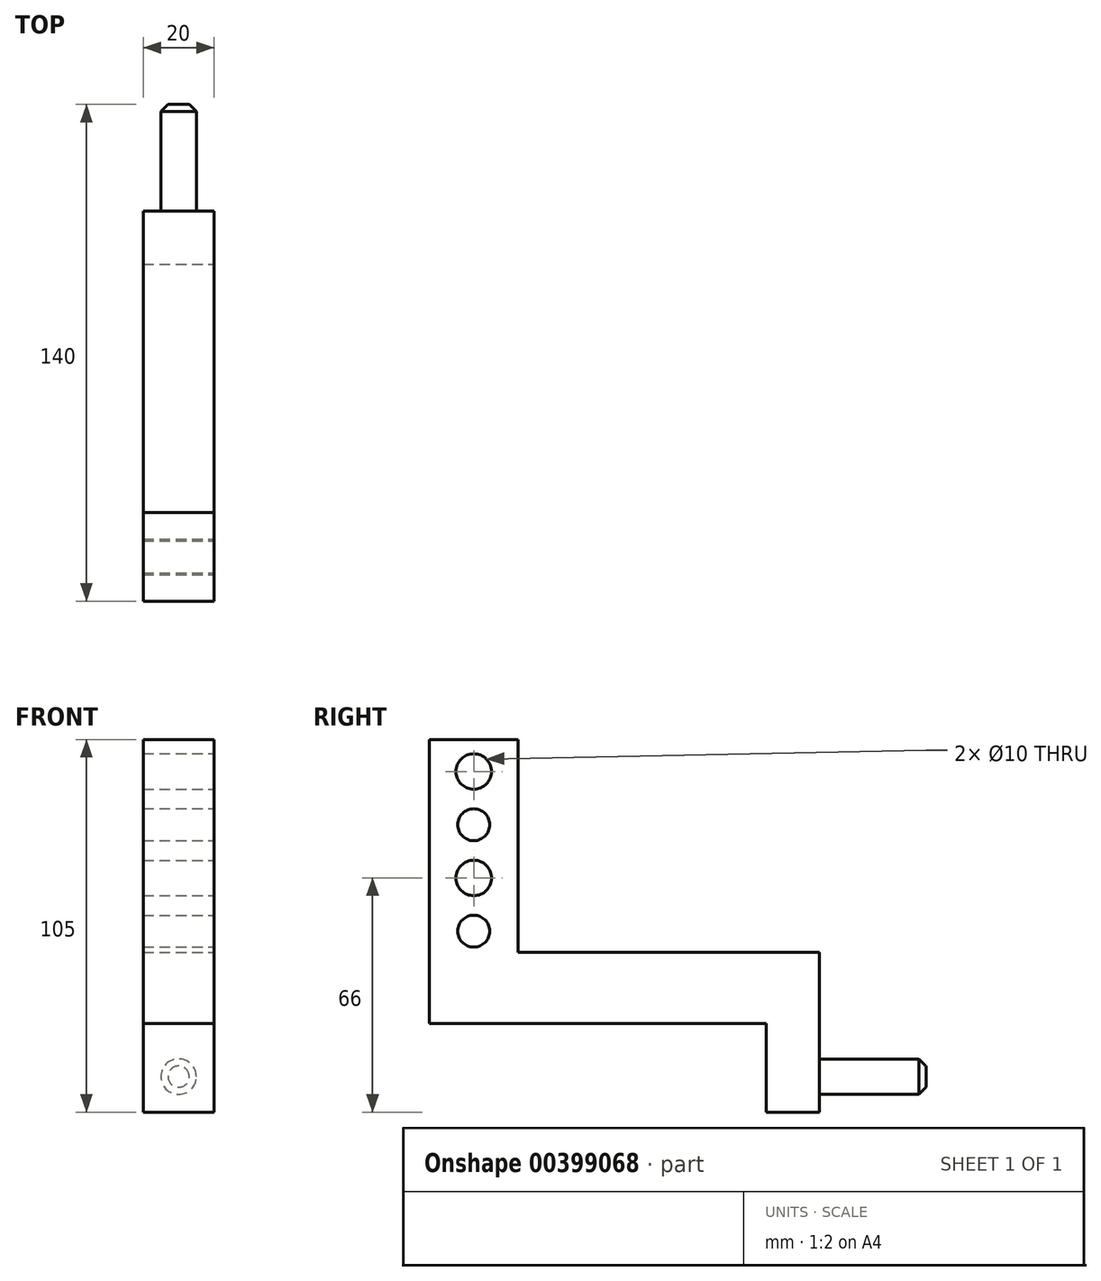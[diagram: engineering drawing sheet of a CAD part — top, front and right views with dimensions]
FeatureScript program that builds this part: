
annotation { "Feature Type Name" : "Feature", "Feature Type Description" : "" }
export const myFeature = defineFeature(function(context is Context, id is Id, definition is map)
    precondition{}
    {
        {
            var Q0;
            Q0=qCreatedBy(makeId("Top.planeOp"),FACE);
            var sketch = newSketch(context, id + "F0", { "sketchPlane" : qUnion([Q0])});
            skLineSegment(sketch, "E0.bottom", {"start": v(0, 0) * mm, "end": v(20, 0) * mm});
            skLineSegment(sketch, "E0.top", {"start": v(0, -25) * mm, "end": v(20, -25) * mm});
            skLineSegment(sketch, "E0.left", {"start": v(0, 0) * mm, "end": v(0, -25) * mm});
            skLineSegment(sketch, "E0.right", {"start": v(20, 0) * mm, "end": v(20, -25) * mm});
            skSolve(sketch);
        }
        {
            var Q0;
            Q0 = qSketchRegion(id + "F0", true);
            extrude(context, id + "F1", {"entities" : qUnion([Q0]), "depth" : 80 * mm});
        }
        {
            var Q0;
            Q0=makeQuery(id+"F1.opExtrude","SWEPT_FACE",FACE,{"disambiguationData":[OSD([sQuery(id+"F0.wireOp",EDGE,"E0.right")])]});
            var sketch = newSketch(context, id + "F2", { "sketchPlane" : qUnion([Q0])});
            skLineSegment(sketch, "E1", {"start": v(-12.5, 80) * mm, "end": v(-12.5, 71) * mm, "construction": true});
            skPoint(sketch, "E1.endSnap0", {"position": v(-12.5, 80) * mm});
            skLineSegment(sketch, "E2", {"start": v(-12.5, 71) * mm, "end": v(-12.5, 56) * mm, "construction": true});
            skLineSegment(sketch, "E3", {"start": v(-12.5, 56) * mm, "end": v(-12.5, 41) * mm, "construction": true});
            skLineSegment(sketch, "E4", {"start": v(-12.5, 41) * mm, "end": v(-12.5, 26) * mm, "construction": true});
            skLineSegment(sketch, "E5", {"start": v(-12.5, 26) * mm, "end": v(-12.5, 0) * mm, "construction": true});
            skCircle(sketch, "E6", {"center": v(-12.5, 71) * mm, "radius": 5 * mm});
            skCircle(sketch, "E7", {"center": v(-12.5, 56) * mm, "radius": 4.5 * mm});
            skCircle(sketch, "E8", {"center": v(-12.5, 41) * mm, "radius": 5 * mm});
            skCircle(sketch, "E9", {"center": v(-12.5, 26) * mm, "radius": 4.5 * mm});
            skSolve(sketch);
        }
        {
            var Q0;
            Q0 = qSketchRegion(id + "F2", true);
            extrude(context, id + "F3", {"entities" : qUnion([Q0]), "operationType" : NewBodyOperationType.REMOVE, "oppositeDirection" : true, "depth" : 25 * mm});
        }
        {
            var Q0;
            Q0=makeQuery(id+"F1.opExtrude","SWEPT_FACE",FACE,{"disambiguationData":[OSD([sQuery(id+"F0.wireOp",EDGE,"E0.bottom")])]});
            var sketch = newSketch(context, id + "F4", { "sketchPlane" : qUnion([Q0])});
            skLineSegment(sketch, "E10.bottom", {"start": v(0, 0) * mm, "end": v(-20, 0) * mm});
            skLineSegment(sketch, "E10.top", {"start": v(0, 20) * mm, "end": v(-20, 20) * mm});
            skLineSegment(sketch, "E10.left", {"start": v(0, 0) * mm, "end": v(0, 20) * mm});
            skLineSegment(sketch, "E10.right", {"start": v(-20, 0) * mm, "end": v(-20, 20) * mm});
            skSolve(sketch);
        }
        {
            var Q0;
            Q0=makeQuery(id+"F4.imprint","IMPRINT",FACE,{"disambiguationData":[TD([[makeQuery(id+"F4.imprint","IMPRINT",EDGE,{"derivedFrom":sQuery(id+"F4.wireOp",EDGE,"E10.bottom")}),-1.0]])]});
            extrude(context, id + "F5", {"entities" : qUnion([Q0]), "operationType" : NewBodyOperationType.ADD, "depth" : 70 * mm});
        }
        {
            var Q0;
            Q0=makeQuery(id+"F5.opExtrude","CAP_FACE",FACE,{"disambiguationData":[OSD([sQuery(id+"F4.wireOp",EDGE,"E10.bottom"),sQuery(id+"F4.wireOp",EDGE,"E10.top"),sQuery(id+"F4.wireOp",EDGE,"E10.left"),sQuery(id+"F4.wireOp",EDGE,"E10.right")])],"isStart":false});
            var sketch = newSketch(context, id + "F6", { "sketchPlane" : qUnion([Q0])});
            skLineSegment(sketch, "E11.bottom", {"start": v(-20, 20) * mm, "end": v(0, 20) * mm});
            skLineSegment(sketch, "E11.top", {"start": v(-20, -25) * mm, "end": v(0, -25) * mm});
            skLineSegment(sketch, "E11.left", {"start": v(-20, 20) * mm, "end": v(-20, -25) * mm});
            skLineSegment(sketch, "E11.right", {"start": v(0, 20) * mm, "end": v(0, -25) * mm});
            skSolve(sketch);
        }
        {
            var Q0;
            Q0 = qSketchRegion(id + "F6", true);
            extrude(context, id + "F7", {"entities" : qUnion([Q0]), "operationType" : NewBodyOperationType.ADD, "depth" : 15 * mm});
        }
        {
            var Q0;
            Q0=makeQuery(id+"F7.opExtrude","CAP_FACE",FACE,{"disambiguationData":[OSD([sQuery(id+"F6.wireOp",EDGE,"E11.bottom"),sQuery(id+"F6.wireOp",EDGE,"E11.top"),sQuery(id+"F6.wireOp",EDGE,"E11.left"),sQuery(id+"F6.wireOp",EDGE,"E11.right")])],"isStart":false});
            var sketch = newSketch(context, id + "F8", { "sketchPlane" : qUnion([Q0])});
            skLineSegment(sketch, "E12", {"start": v(-10, -25) * mm, "end": v(-10, -15) * mm, "construction": true});
            skCircle(sketch, "E13", {"center": v(-10, -15) * mm, "radius": 5 * mm});
            skSolve(sketch);
        }
        {
            var Q0;
            Q0 = qSketchRegion(id + "F8", true);
            extrude(context, id + "F9", {"entities" : qUnion([Q0]), "operationType" : NewBodyOperationType.ADD, "depth" : 30 * mm});
        }
        {
            var Q0;
            Q0=makeQuery(id+"F9.opExtrude","CAP_EDGE",EDGE,{"disambiguationData":[OSD([sQuery(id+"F8.wireOp",EDGE,"E13")])],"isStart":false});
            chamfer(context, id + "F10", {"entities" : qUnion([Q0]), "width" : 2 * mm, "tangentPropagation" : true});
        }
    });
